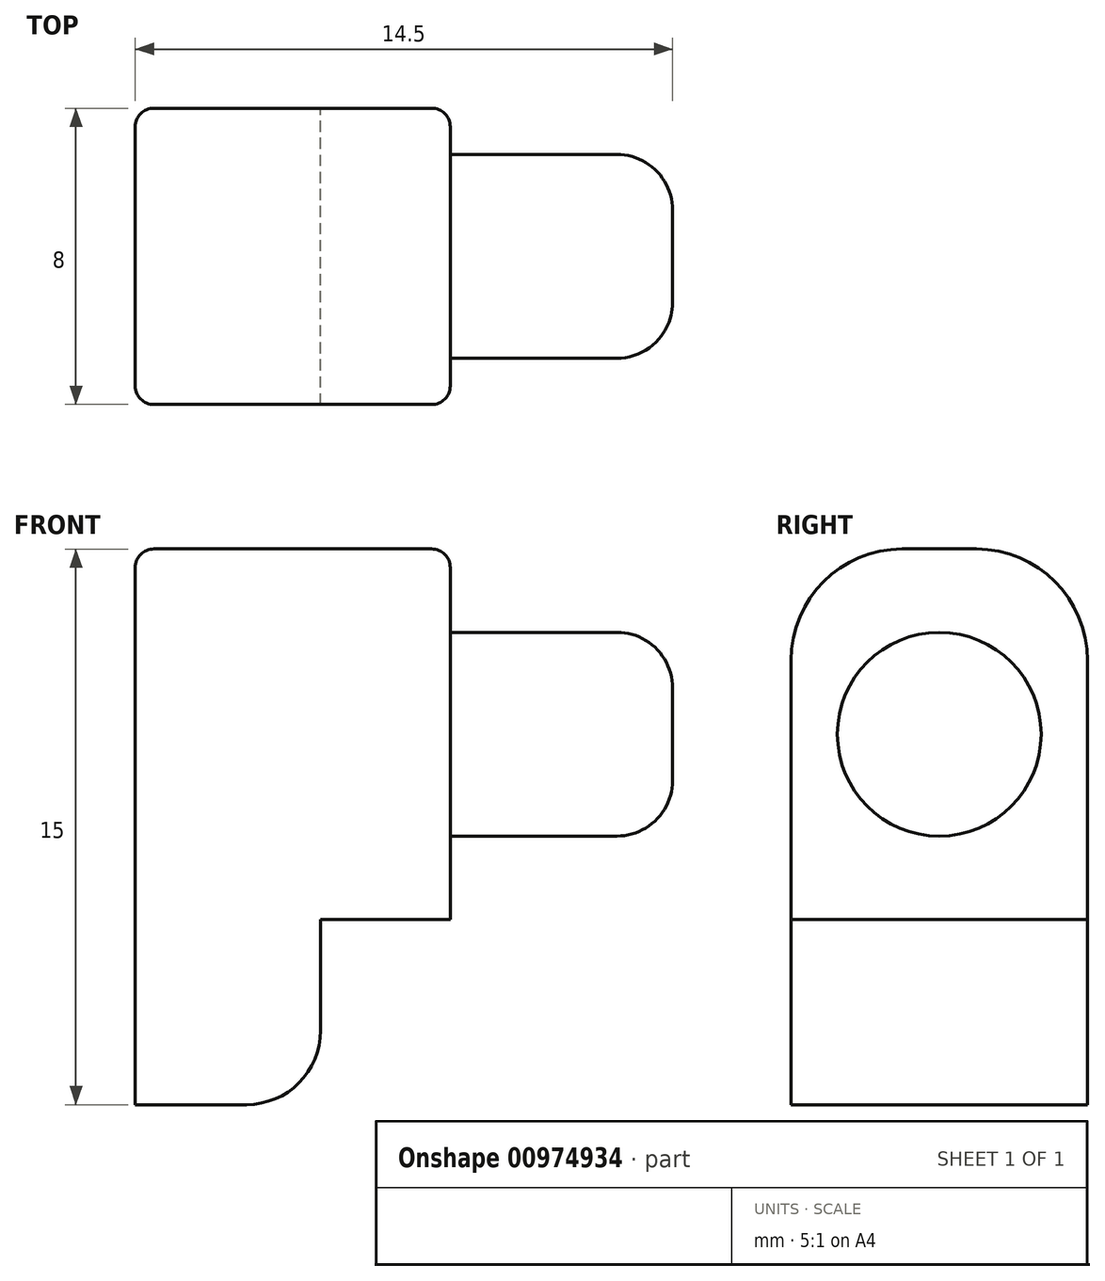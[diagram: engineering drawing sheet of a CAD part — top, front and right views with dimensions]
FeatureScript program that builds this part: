
annotation { "Feature Type Name" : "Feature", "Feature Type Description" : "" }
export const myFeature = defineFeature(function(context is Context, id is Id, definition is map)
    precondition{}
    {
        {
            var Q0;
            Q0=qCreatedBy(makeId("Front.planeOp"),FACE);
            var sketch = newSketch(context, id + "F0", { "sketchPlane" : qUnion([Q0])});
            skLineSegment(sketch, "E0.bottom", {"start": v(-3.5, 12.18) * mm, "end": v(5, 12.18) * mm});
            skLineSegment(sketch, "E0.top", {"start": v(-3.5, -2.82) * mm, "end": v(-0.5, -2.82) * mm});
            skLineSegment(sketch, "E0.left", {"start": v(-3.5, 12.18) * mm, "end": v(-3.5, -2.82) * mm});
            skPoint(sketch, "E1", {"position": v(5, 2.18) * mm});
            skLineSegment(sketch, "E2", {"start": v(5, 2.18) * mm, "end": v(1.5, 2.18) * mm});
            skLineSegment(sketch, "E3", {"start": v(1.5, 2.18) * mm, "end": v(1.5, -0.82) * mm});
            skArc(sketch, "E4.filletArc", {"start": v(-0.5, -2.82) * mm, "mid": v(0.91, -2.23) * mm, "end": v(1.5, -0.82) * mm});
            skLineSegment(sketch, "E5", {"start": v(5, 2.18) * mm, "end": v(5, 12.18) * mm});
            skSolve(sketch);
        }
        {
            var Q0;
            Q0 = qSketchRegion(id + "F0", true);
            extrude(context, id + "F1", {"entities" : qUnion([Q0]), "depth" : 8 * mm, "offsetDistance" : 25 * mm});
        }
        {
            var Q0;
            Q0=makeQuery(id+"F1.opExtrude","SWEPT_FACE",FACE,{"disambiguationData":[OSD([sQuery(id+"F0.wireOp",EDGE,"E5")])]});
            var sketch = newSketch(context, id + "F2", { "sketchPlane" : qUnion([Q0])});
            skCircle(sketch, "E6", {"center": v(-4, 7.18) * mm, "radius": 2.75 * mm});
            skSolve(sketch);
        }
        {
            var Q0;
            Q0=makeQuery(id+"F2.imprint","IMPRINT",FACE,{"disambiguationData":[TD([[makeQuery(id+"F2.imprint","IMPRINT",EDGE,{"derivedFrom":sQuery(id+"F2.wireOp",EDGE,"E6")}),1.0]])]});
            extrude(context, id + "F3", {"entities" : qUnion([Q0]), "operationType" : NewBodyOperationType.ADD, "depth" : 6 * mm, "offsetDistance" : 25 * mm});
        }
        {
            var Q0;
            Q0=makeQuery(id+"F3.opExtrude","CAP_EDGE",EDGE,{"disambiguationData":[OSD([sQuery(id+"F2.wireOp",EDGE,"E6")])],"isStart":false});
            fillet(context, id + "F4", {"entities" : qUnion([Q0]), "radius" : 1.5 * mm, "tangentPropagation" : true, "allowEdgeOverflow" : false});
        }
        {
            var Q0;
            Q0=makeQuery(id+"F1.opExtrude","CAP_EDGE",EDGE,{"disambiguationData":[OSD([sQuery(id+"F0.wireOp",EDGE,"E0.bottom")])],"isStart":true});
            var Q1;
            Q1=makeQuery(id+"F1.opExtrude","CAP_EDGE",EDGE,{"disambiguationData":[OSD([sQuery(id+"F0.wireOp",EDGE,"E0.bottom")])],"isStart":false});
            fillet(context, id + "F5", {"entities" : qUnion([Q0, Q1]), "radius" : 3 * mm, "tangentPropagation" : true, "allowEdgeOverflow" : false});
        }
        {
            var Q0;
            Q0=makeQuery(id+"F1.opExtrude","CAP_EDGE",EDGE,{"disambiguationData":[OSD([sQuery(id+"F0.wireOp",EDGE,"E5")])],"isStart":false});
            var Q1;
            Q1=makeQuery(id+"F5.opFillet","BLEND_EDGE",EDGE,{"blendedFrom":[makeQuery(id+"F1.opExtrude","CAP_EDGE",EDGE,{"disambiguationData":[OSD([sQuery(id+"F0.wireOp",EDGE,"E0.bottom")])],"isStart":false}),makeQuery(id+"F1.opExtrude","SWEPT_FACE",FACE,{"disambiguationData":[OSD([sQuery(id+"F0.wireOp",EDGE,"E5")])]})],"blendedInto":[makeQuery(id+"F1.opExtrude","SWEPT_FACE",FACE,{"disambiguationData":[OSD([sQuery(id+"F0.wireOp",EDGE,"E5")])]})]});
            var Q2;
            Q2=makeQuery(id+"F1.opExtrude","SWEPT_EDGE",EDGE,{"disambiguationData":[OSD([sQuery(id+"F0.wireOp",EDGE,"E0.bottom"),sQuery(id+"F0.wireOp",EDGE,"E5")])]});
            var Q3;
            Q3=makeQuery(id+"F5.opFillet","BLEND_EDGE",EDGE,{"blendedFrom":[makeQuery(id+"F1.opExtrude","CAP_EDGE",EDGE,{"disambiguationData":[OSD([sQuery(id+"F0.wireOp",EDGE,"E0.bottom")])],"isStart":true}),makeQuery(id+"F1.opExtrude","SWEPT_FACE",FACE,{"disambiguationData":[OSD([sQuery(id+"F0.wireOp",EDGE,"E5")])]})],"blendedInto":[makeQuery(id+"F1.opExtrude","SWEPT_FACE",FACE,{"disambiguationData":[OSD([sQuery(id+"F0.wireOp",EDGE,"E5")])]})]});
            var Q4;
            Q4=makeQuery(id+"F1.opExtrude","CAP_EDGE",EDGE,{"disambiguationData":[OSD([sQuery(id+"F0.wireOp",EDGE,"E5")])],"isStart":true});
            var Q5;
            Q5=makeQuery(id+"F1.opExtrude","CAP_EDGE",EDGE,{"disambiguationData":[OSD([sQuery(id+"F0.wireOp",EDGE,"E0.left")])],"isStart":false});
            var Q6;
            Q6=makeQuery(id+"F5.opFillet","BLEND_EDGE",EDGE,{"blendedFrom":[makeQuery(id+"F1.opExtrude","CAP_EDGE",EDGE,{"disambiguationData":[OSD([sQuery(id+"F0.wireOp",EDGE,"E0.bottom")])],"isStart":false}),makeQuery(id+"F1.opExtrude","SWEPT_FACE",FACE,{"disambiguationData":[OSD([sQuery(id+"F0.wireOp",EDGE,"E0.left")])]})],"blendedInto":[makeQuery(id+"F1.opExtrude","SWEPT_FACE",FACE,{"disambiguationData":[OSD([sQuery(id+"F0.wireOp",EDGE,"E0.left")])]})]});
            fillet(context, id + "F6", {"entities" : qUnion([Q0, Q1, Q2, Q3, Q4, Q5, Q6]), "radius" : 0.5 * mm, "tangentPropagation" : true, "allowEdgeOverflow" : false});
        }
    });
